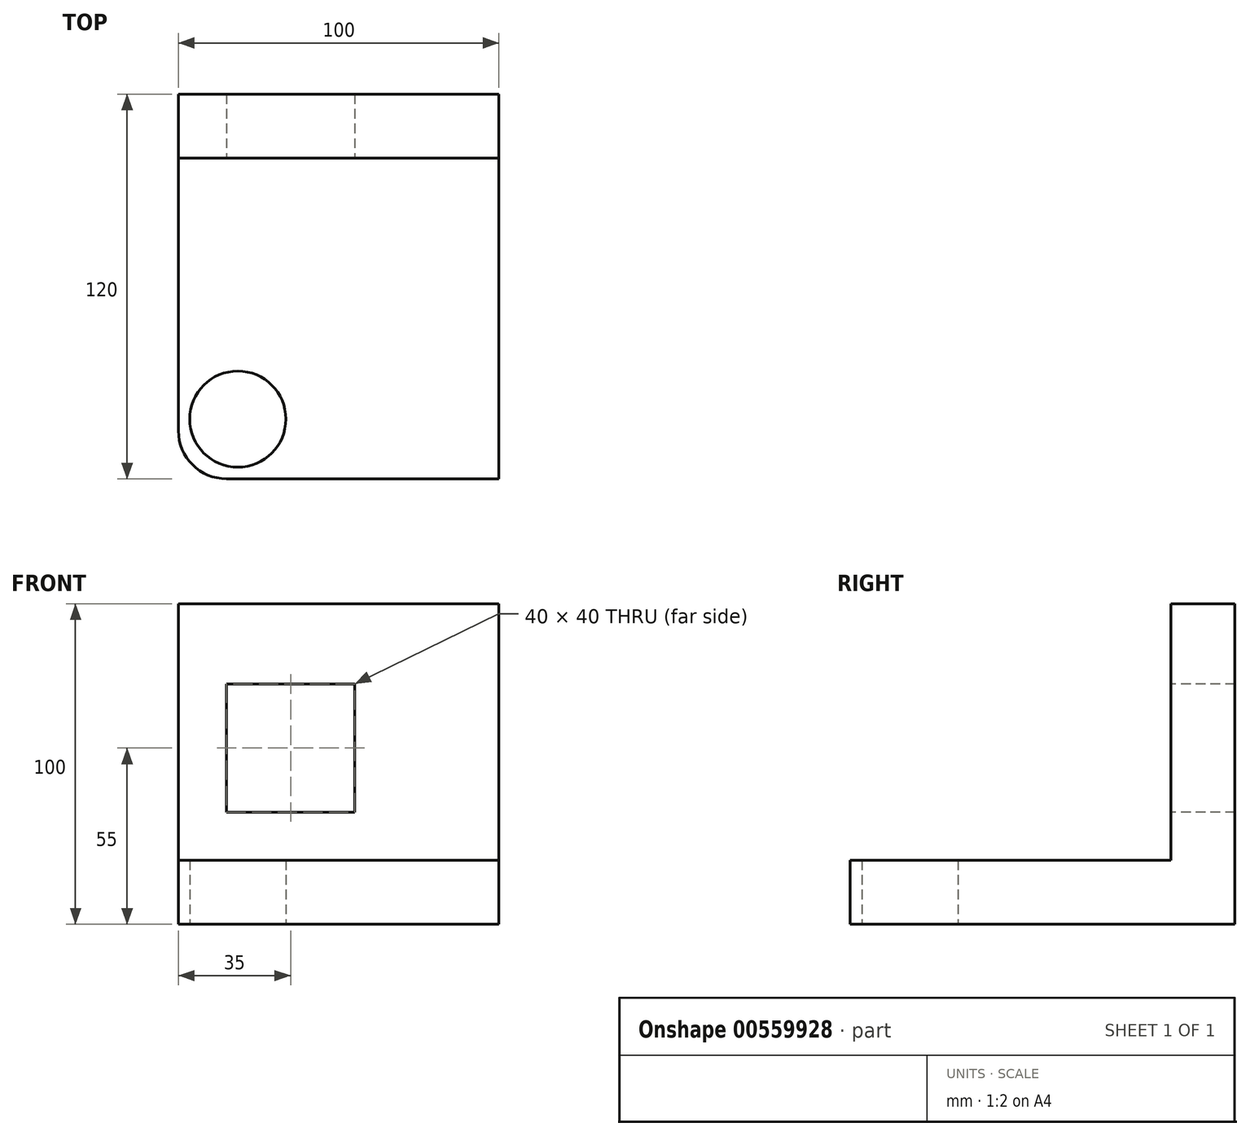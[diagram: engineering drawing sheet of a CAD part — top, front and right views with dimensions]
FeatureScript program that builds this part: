
annotation { "Feature Type Name" : "Feature", "Feature Type Description" : "" }
export const myFeature = defineFeature(function(context is Context, id is Id, definition is map)
    precondition{}
    {
        {
            var Q0;
            Q0=qCreatedBy(makeId("Top.planeOp"),FACE);
            var sketch = newSketch(context, id + "F0", { "sketchPlane" : qUnion([Q0])});
            skLineSegment(sketch, "E0.bottom", {"start": v(0, 0) * mm, "end": v(100, 0) * mm});
            skLineSegment(sketch, "E0.top", {"start": v(15, -100) * mm, "end": v(100, -100) * mm});
            skLineSegment(sketch, "E0.left", {"start": v(0, 0) * mm, "end": v(0, -85) * mm});
            skLineSegment(sketch, "E0.right", {"start": v(100, 0) * mm, "end": v(100, -100) * mm});
            skCircle(sketch, "E1", {"center": v(18.5, -81.38) * mm, "radius": 15 * mm});
            skPoint(sketch, "E2", {"position": v(50, -100) * mm});
            skPoint(sketch, "E3.visualSharp", {"position": v(0, -100) * mm});
            skArc(sketch, "E3.filletArc", {"start": v(0, -85) * mm, "mid": v(4.4, -95.6) * mm, "end": v(15, -100) * mm});
            skLineSegment(sketch, "E4", {"start": v(0, -100) * mm, "end": v(15, -85) * mm});
            skSolve(sketch);
        }
        {
            var Q0;
            Q0=makeQuery(id+"F0.imprint","IMPRINT",FACE,{"disambiguationData":[TD([[makeQuery(id+"F0.imprint","IMPRINT",EDGE,{"derivedFrom":sQuery(id+"F0.wireOp",EDGE,"E0.bottom")}),-1.0]])]});
            extrude(context, id + "F1", {"entities" : qUnion([Q0]), "depth" : 20 * mm, "offsetDistance" : 25 * mm});
        }
        {
            var Q0;
            Q0=qCreatedBy(makeId("Front.planeOp"),FACE);
            var sketch = newSketch(context, id + "F2", { "sketchPlane" : qUnion([Q0])});
            skLineSegment(sketch, "E5.bottom", {"start": v(0, 0) * mm, "end": v(100, 0) * mm});
            skLineSegment(sketch, "E5.top", {"start": v(0, 100) * mm, "end": v(100, 100) * mm});
            skLineSegment(sketch, "E5.left", {"start": v(0, 0) * mm, "end": v(0, 100) * mm});
            skLineSegment(sketch, "E5.right", {"start": v(100, 0) * mm, "end": v(100, 100) * mm});
            skLineSegment(sketch, "E6.bottom", {"start": v(15, 35) * mm, "end": v(55, 35) * mm});
            skLineSegment(sketch, "E6.top", {"start": v(15, 75) * mm, "end": v(55, 75) * mm});
            skLineSegment(sketch, "E6.left", {"start": v(15, 35) * mm, "end": v(15, 75) * mm});
            skLineSegment(sketch, "E6.right", {"start": v(55, 35) * mm, "end": v(55, 75) * mm});
            skSolve(sketch);
        }
        {
            var Q0;
            Q0=makeQuery(id+"F2.imprint","IMPRINT",FACE,{"disambiguationData":[TD([[makeQuery(id+"F2.imprint","IMPRINT",EDGE,{"derivedFrom":sQuery(id+"F2.wireOp",EDGE,"E5.bottom")}),1.0]])]});
            extrude(context, id + "F3", {"entities" : qUnion([Q0]), "operationType" : NewBodyOperationType.ADD, "oppositeDirection" : true, "depth" : 20 * mm, "offsetDistance" : 25 * mm});
        }
    });
